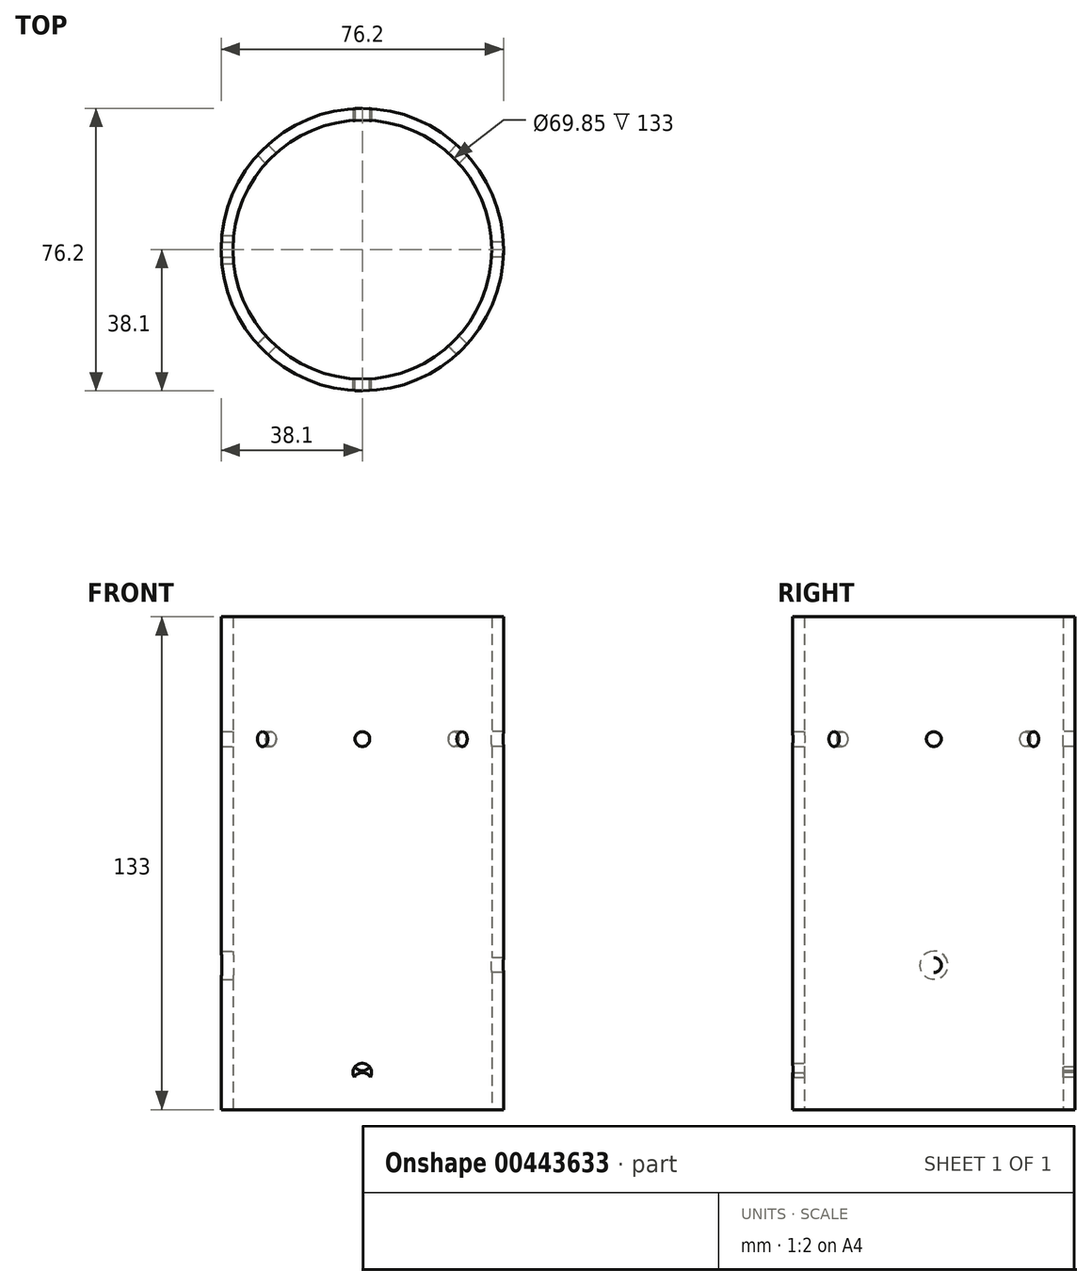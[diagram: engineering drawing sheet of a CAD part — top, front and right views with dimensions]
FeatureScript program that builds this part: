
annotation { "Feature Type Name" : "Feature", "Feature Type Description" : "" }
export const myFeature = defineFeature(function(context is Context, id is Id, definition is map)
    precondition{}
    {
        {
            var Q0;
            Q0=qCreatedBy(makeId("Top.planeOp"),FACE);
            var sketch = newSketch(context, id + "F0", { "sketchPlane" : qUnion([Q0])});
            skCircle(sketch, "E0", {"center": v(0, 0) * mm, "radius": 38.1 * mm});
            skCircle(sketch, "E1", {"center": v(0, 0) * mm, "radius": 34.92 * mm});
            skSolve(sketch);
        }
        {
            var Q0;
            Q0 = qSketchRegion(id + "F0", true);
            extrude(context, id + "F1", {"entities" : qUnion([Q0]), "depth" : 133 * mm});
        }
        {
            var Q0;
            Q0=qCreatedBy(makeId("Front.planeOp"),FACE);
            var sketch = newSketch(context, id + "F2", { "sketchPlane" : qUnion([Q0])});
            skCircle(sketch, "E2", {"center": v(0, 100) * mm, "radius": 2 * mm});
            skLineSegment(sketch, "E3", {"start": v(0, -14.07) * mm, "end": v(0, 149.8) * mm, "construction": true});
            skCircle(sketch, "E4", {"center": v(0, 10) * mm, "radius": 2.5 * mm});
            skCircle(sketch, "E5", {"center": v(0, 7.5) * mm, "radius": 2.5 * mm});
            skCircle(sketch, "E6", {"center": v(0, 13) * mm, "radius": 2.5 * mm});
            skSolve(sketch);
        }
        {
            var Q0;
            Q0=makeQuery(id+"F2.imprint","IMPRINT",FACE,{"disambiguationData":[TD([[makeQuery(id+"F2.imprint","IMPRINT",EDGE,{"derivedFrom":sQuery(id+"F2.wireOp",EDGE,"E2")}),1.0]])]});
            extrude(context, id + "F3", {"entities" : qUnion([Q0]), "operationType" : NewBodyOperationType.REMOVE, "oppositeDirection" : true, "depth" : 100 * mm});
        }
        {
            var Q0;
            Q0=makeQuery(id+"F2.imprint","IMPRINT",FACE,{"disambiguationData":[TD([[makeQuery(id+"F2.imprint","IMPRINT",EDGE,{"derivedFrom":sQuery(id+"F2.wireOp",EDGE,"E2")}),1.0]])]});
            extrude(context, id + "F4", {"entities" : qUnion([Q0]), "operationType" : NewBodyOperationType.REMOVE, "depth" : 100 * mm});
        }
        {
            var Q0;
            Q0=qCreatedBy(makeId("Right.planeOp"),FACE);
            var sketch = newSketch(context, id + "F5", { "sketchPlane" : qUnion([Q0])});
            skCircle(sketch, "E7", {"center": v(0, 100) * mm, "radius": 2 * mm});
            skLineSegment(sketch, "E8", {"start": v(0, 0) * mm, "end": v(0, 39) * mm});
            skCircle(sketch, "E9", {"center": v(0, 39) * mm, "radius": 3.81 * mm});
            skCircle(sketch, "E10", {"center": v(0, 39) * mm, "radius": 2 * mm});
            skSolve(sketch);
        }
        {
            var Q0;
            Q0=makeQuery(id+"F5.imprint","IMPRINT",FACE,{"disambiguationData":[TD([[makeQuery(id+"F5.imprint","IMPRINT",EDGE,{"derivedFrom":sQuery(id+"F5.wireOp",EDGE,"E7")}),1.0]])]});
            extrude(context, id + "F6", {"entities" : qUnion([Q0]), "operationType" : NewBodyOperationType.REMOVE, "depth" : 100 * mm});
        }
        {
            var Q0;
            Q0=makeQuery(id+"F5.imprint","IMPRINT",FACE,{"disambiguationData":[TD([[makeQuery(id+"F5.imprint","IMPRINT",EDGE,{"derivedFrom":sQuery(id+"F5.wireOp",EDGE,"E7")}),1.0]])]});
            extrude(context, id + "F7", {"entities" : qUnion([Q0]), "operationType" : NewBodyOperationType.REMOVE, "oppositeDirection" : true, "depth" : 100 * mm});
        }
        {
            var Q0;
            Q0=qCreatedBy(makeId("Top.planeOp"),FACE);
            var sketch = newSketch(context, id + "F8", { "sketchPlane" : qUnion([Q0])});
            skLineSegment(sketch, "E11", {"start": v(0, 57.08) * mm, "end": v(0, -51.25) * mm, "construction": true});
            skCircle(sketch, "E12.cCircle", {"center": v(0, 0) * mm, "radius": 18.26 * mm, "construction": true});
            skLineSegment(sketch, "E12.0", {"start": v(-7.56, 18.26) * mm, "end": v(7.56, 18.26) * mm});
            skLineSegment(sketch, "E12.1", {"start": v(7.56, 18.26) * mm, "end": v(18.26, 7.56) * mm});
            skLineSegment(sketch, "E12.2", {"start": v(18.26, 7.56) * mm, "end": v(18.26, -7.56) * mm});
            skLineSegment(sketch, "E12.3", {"start": v(18.26, -7.56) * mm, "end": v(7.56, -18.26) * mm});
            skLineSegment(sketch, "E12.4", {"start": v(7.56, -18.26) * mm, "end": v(-7.56, -18.26) * mm});
            skLineSegment(sketch, "E12.5", {"start": v(-7.56, -18.26) * mm, "end": v(-18.26, -7.56) * mm});
            skLineSegment(sketch, "E12.6", {"start": v(-18.26, -7.56) * mm, "end": v(-18.26, 7.56) * mm});
            skLineSegment(sketch, "E12.7", {"start": v(-18.26, 7.56) * mm, "end": v(-7.56, 18.26) * mm});
            skPoint(sketch, "E12.0.midPoint", {"position": v(0, 18.26) * mm});
            skSolve(sketch);
        }
        {
            var Q0;
            Q0=sQuery(id+"F8.wireOp",EDGE,"E12.5");
            cPlane(context, id + "F9", {"entities" : qUnion([Q0]), "cplaneType" : CPlaneType.MID_PLANE, "offset" : 100 * mm, "oppositeDirection" : true, "width" : 150 * mm, "height" : 150 * mm});
        }
        {
            var Q0;
            Q0=sQuery(id+"F8.wireOp",EDGE,"E12.3");
            cPlane(context, id + "F10", {"entities" : qUnion([Q0]), "cplaneType" : CPlaneType.MID_PLANE, "offset" : 25 * mm, "width" : 150 * mm, "height" : 150 * mm});
        }
        {
            var Q0;
            Q0=qCreatedBy(id+"F9.planeOp",FACE);
            var sketch = newSketch(context, id + "F11", { "sketchPlane" : qUnion([Q0])});
            skCircle(sketch, "E13", {"center": v(0, 100) * mm, "radius": 2 * mm});
            skSolve(sketch);
        }
        {
            var Q0;
            Q0=makeQuery(id+"F11.imprint","IMPRINT",FACE,{"disambiguationData":[TD([[makeQuery(id+"F11.imprint","IMPRINT",EDGE,{"derivedFrom":sQuery(id+"F11.wireOp",EDGE,"E13")}),1.0]])]});
            extrude(context, id + "F12", {"entities" : qUnion([Q0]), "operationType" : NewBodyOperationType.REMOVE, "depth" : 100 * mm});
        }
        {
            var Q0;
            Q0 = qSketchRegion(id + "F11", true);
            extrude(context, id + "F13", {"entities" : qUnion([Q0]), "operationType" : NewBodyOperationType.REMOVE, "oppositeDirection" : true, "depth" : 100 * mm});
        }
        {
            var Q0;
            Q0=qCreatedBy(id+"F10.planeOp",FACE);
            var sketch = newSketch(context, id + "F14", { "sketchPlane" : qUnion([Q0])});
            skCircle(sketch, "E14", {"center": v(0, 100) * mm, "radius": 2 * mm});
            skSolve(sketch);
        }
        {
            var Q0;
            Q0=makeQuery(id+"F14.imprint","IMPRINT",FACE,{"disambiguationData":[TD([[makeQuery(id+"F14.imprint","IMPRINT",EDGE,{"derivedFrom":sQuery(id+"F14.wireOp",EDGE,"E14")}),1.0]])]});
            extrude(context, id + "F15", {"entities" : qUnion([Q0]), "operationType" : NewBodyOperationType.REMOVE, "oppositeDirection" : true, "depth" : 100 * mm});
        }
        {
            var Q0;
            Q0 = qSketchRegion(id + "F14", true);
            extrude(context, id + "F16", {"entities" : qUnion([Q0]), "operationType" : NewBodyOperationType.REMOVE, "depth" : 100 * mm});
        }
        {
            var Q0;
            {var subQ0=sQuery(id+"F2.wireOp",EDGE,"E5");var subQ1=sQuery(id+"F2.wireOp",EDGE,"E4");var subQ2=makeQuery(id+"F2.imprint","INTERSECT",VERTEX,{"disambiguationData":[OD(0.0)],"derivedFrom":[subQ1,subQ0]});Q0=makeQuery(id+"F2.imprint","IMPRINT",FACE,{"disambiguationData":[TD([[makeQuery(id+"F2.imprint","IMPRINT",EDGE,{"disambiguationData":[TD([[subQ2,-1.0]])],"derivedFrom":subQ1}),1.0]])]});}
            var Q1;
            {var subQ0=sQuery(id+"F2.wireOp",EDGE,"E6");var subQ1=sQuery(id+"F2.wireOp",EDGE,"E4");var subQ2=makeQuery(id+"F2.imprint","INTERSECT",VERTEX,{"disambiguationData":[OD(0.0)],"derivedFrom":[subQ1,subQ0]});Q1=makeQuery(id+"F2.imprint","IMPRINT",FACE,{"disambiguationData":[TD([[makeQuery(id+"F2.imprint","IMPRINT",EDGE,{"disambiguationData":[TD([[subQ2,-1.0]])],"derivedFrom":subQ1}),1.0]])]});}
            var Q2;
            {var subQ0=sQuery(id+"F2.wireOp",EDGE,"E6");var subQ1=sQuery(id+"F2.wireOp",EDGE,"E4");var subQ2=makeQuery(id+"F2.imprint","INTERSECT",VERTEX,{"disambiguationData":[OD(0.0)],"derivedFrom":[subQ1,subQ0]});Q2=makeQuery(id+"F2.imprint","IMPRINT",FACE,{"disambiguationData":[TD([[makeQuery(id+"F2.imprint","IMPRINT",EDGE,{"disambiguationData":[TD([[subQ2,1.0]])],"derivedFrom":subQ1}),1.0]])]});}
            var Q3;
            {var subQ0=sQuery(id+"F2.wireOp",EDGE,"E6");var subQ1=sQuery(id+"F2.wireOp",EDGE,"E4");var subQ2=makeQuery(id+"F2.imprint","INTERSECT",VERTEX,{"disambiguationData":[OD(1.0)],"derivedFrom":[subQ1,subQ0]});Q3=makeQuery(id+"F2.imprint","IMPRINT",FACE,{"disambiguationData":[TD([[makeQuery(id+"F2.imprint","IMPRINT",EDGE,{"disambiguationData":[TD([[subQ2,1.0]])],"derivedFrom":subQ1}),1.0]])]});}
            extrude(context, id + "F17", {"entities" : qUnion([Q0, Q1, Q2, Q3]), "operationType" : NewBodyOperationType.REMOVE, "depth" : 40 * mm});
        }
        {
            var Q0;
            {var subQ0=sQuery(id+"F2.wireOp",EDGE,"E6");var subQ1=sQuery(id+"F2.wireOp",EDGE,"E4");var subQ2=makeQuery(id+"F2.imprint","INTERSECT",VERTEX,{"disambiguationData":[OD(0.0)],"derivedFrom":[subQ1,subQ0]});Q0=makeQuery(id+"F2.imprint","IMPRINT",FACE,{"disambiguationData":[TD([[makeQuery(id+"F2.imprint","IMPRINT",EDGE,{"disambiguationData":[TD([[subQ2,1.0]])],"derivedFrom":subQ1}),1.0]])]});}
            var Q1;
            {var subQ0=sQuery(id+"F2.wireOp",EDGE,"E6");var subQ1=sQuery(id+"F2.wireOp",EDGE,"E4");var subQ2=makeQuery(id+"F2.imprint","INTERSECT",VERTEX,{"disambiguationData":[OD(0.0)],"derivedFrom":[subQ1,subQ0]});Q1=makeQuery(id+"F2.imprint","IMPRINT",FACE,{"disambiguationData":[TD([[makeQuery(id+"F2.imprint","IMPRINT",EDGE,{"disambiguationData":[TD([[subQ2,1.0]])],"derivedFrom":subQ1}),-1.0]])]});}
            var Q2;
            {var subQ0=sQuery(id+"F2.wireOp",EDGE,"E5");var subQ1=sQuery(id+"F2.wireOp",EDGE,"E4");var subQ2=makeQuery(id+"F2.imprint","INTERSECT",VERTEX,{"disambiguationData":[OD(0.0)],"derivedFrom":[subQ1,subQ0]});Q2=makeQuery(id+"F2.imprint","IMPRINT",FACE,{"disambiguationData":[TD([[makeQuery(id+"F2.imprint","IMPRINT",EDGE,{"disambiguationData":[TD([[subQ2,-1.0]])],"derivedFrom":subQ1}),1.0]])]});}
            var Q3;
            {var subQ0=sQuery(id+"F2.wireOp",EDGE,"E5");var subQ1=sQuery(id+"F2.wireOp",EDGE,"E4");var subQ2=makeQuery(id+"F2.imprint","INTERSECT",VERTEX,{"disambiguationData":[OD(0.0)],"derivedFrom":[subQ1,subQ0]});Q3=makeQuery(id+"F2.imprint","IMPRINT",FACE,{"disambiguationData":[TD([[makeQuery(id+"F2.imprint","IMPRINT",EDGE,{"disambiguationData":[TD([[subQ2,-1.0]])],"derivedFrom":subQ1}),-1.0]])]});}
            extrude(context, id + "F18", {"entities" : qUnion([Q0, Q1, Q2, Q3]), "operationType" : NewBodyOperationType.REMOVE, "oppositeDirection" : true, "depth" : 40 * mm});
        }
        {
            var Q0;
            Q0=makeQuery(id+"F5.imprint","IMPRINT",FACE,{"disambiguationData":[TD([[makeQuery(id+"F5.imprint","IMPRINT",EDGE,{"derivedFrom":sQuery(id+"F5.wireOp",EDGE,"E10")}),1.0]])]});
            extrude(context, id + "F19", {"entities" : qUnion([Q0]), "operationType" : NewBodyOperationType.REMOVE, "depth" : 40 * mm});
        }
        {
            var Q0;
            Q0=makeQuery(id+"F5.imprint","IMPRINT",FACE,{"disambiguationData":[TD([[makeQuery(id+"F5.imprint","IMPRINT",EDGE,{"derivedFrom":sQuery(id+"F5.wireOp",EDGE,"E9")}),1.0]])]});
            var Q1;
            Q1=makeQuery(id+"F5.imprint","IMPRINT",FACE,{"disambiguationData":[TD([[makeQuery(id+"F5.imprint","IMPRINT",EDGE,{"derivedFrom":sQuery(id+"F5.wireOp",EDGE,"E10")}),1.0]])]});
            extrude(context, id + "F20", {"entities" : qUnion([Q0, Q1]), "operationType" : NewBodyOperationType.REMOVE, "oppositeDirection" : true, "depth" : 40 * mm});
        }
    });
